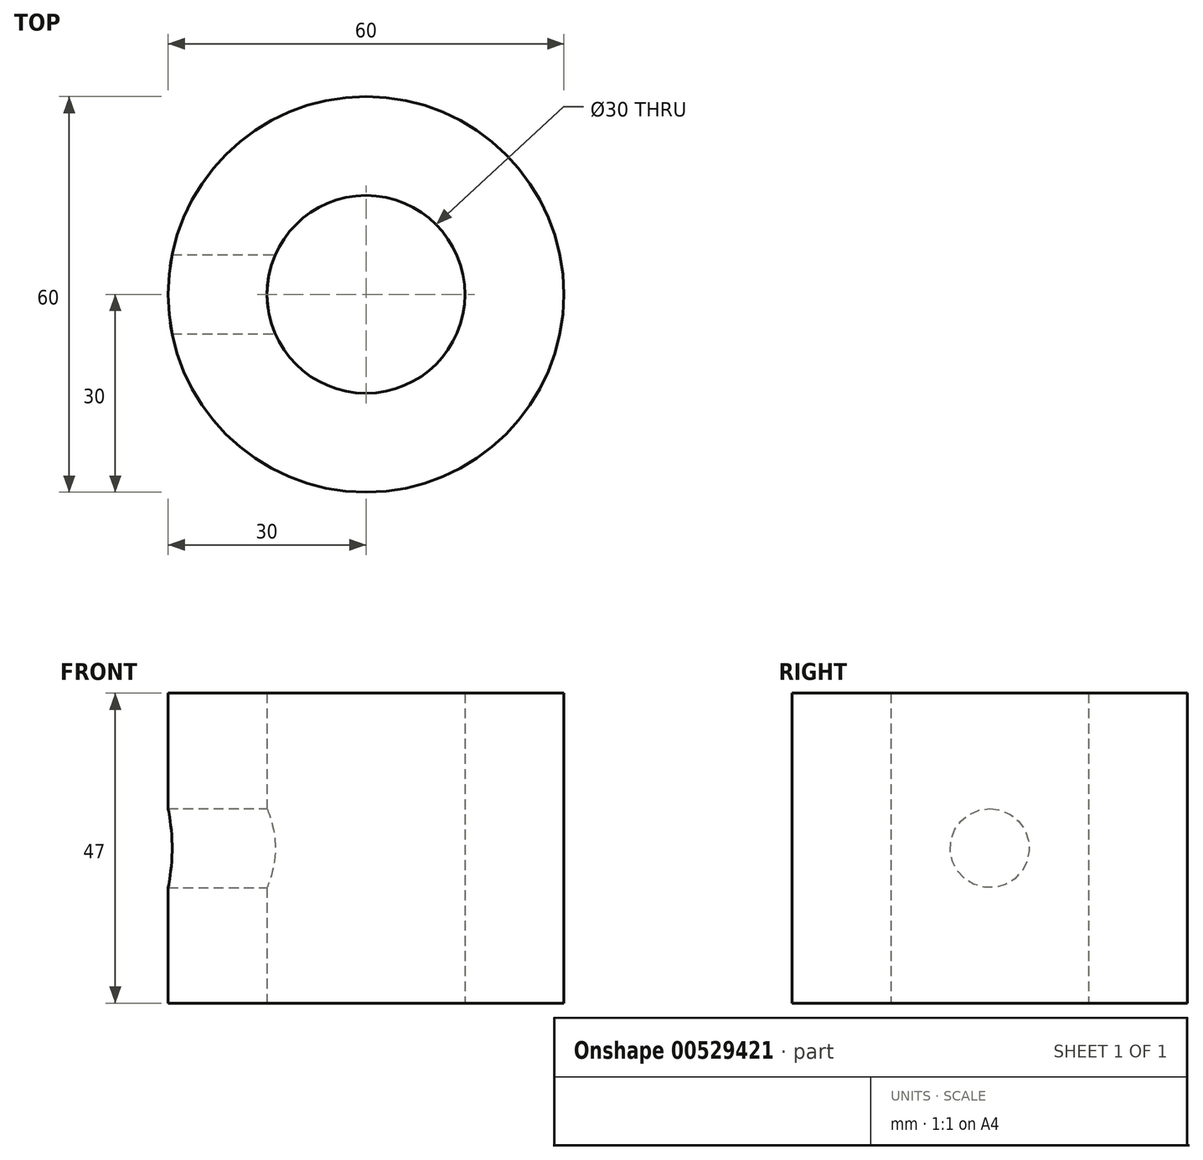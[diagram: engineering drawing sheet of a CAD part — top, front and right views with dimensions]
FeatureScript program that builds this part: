
annotation { "Feature Type Name" : "Feature", "Feature Type Description" : "" }
export const myFeature = defineFeature(function(context is Context, id is Id, definition is map)
    precondition{}
    {
        {
            var Q0;
            Q0=qCreatedBy(makeId("Top.planeOp"),FACE);
            var sketch = newSketch(context, id + "F0", { "sketchPlane" : qUnion([Q0])});
            skCircle(sketch, "E0", {"center": v(0, 0) * mm, "radius": 15 * mm});
            skCircle(sketch, "E1", {"center": v(0, 0) * mm, "radius": 30 * mm});
            skSolve(sketch);
        }
        {
            var Q0;
            Q0=makeQuery(id+"F0.imprint","IMPRINT",FACE,{"disambiguationData":[TD([[makeQuery(id+"F0.imprint","IMPRINT",EDGE,{"derivedFrom":sQuery(id+"F0.wireOp",EDGE,"E0")}),-1.0]])]});
            extrude(context, id + "F1", {"entities" : qUnion([Q0]), "depth" : 47 * mm, "offsetDistance" : 25 * mm});
        }
        {
            var Q0;
            Q0=qCreatedBy(makeId("Right.planeOp"),FACE);
            var sketch = newSketch(context, id + "F2", { "sketchPlane" : qUnion([Q0])});
            skLineSegment(sketch, "E2.0", {"start": v(-30, 47) * mm, "end": v(30, 47) * mm});
            skLineSegment(sketch, "E3", {"start": v(0, 0) * mm, "end": v(0, 23.5) * mm, "construction": true});
            skPoint(sketch, "E4", {"position": v(0, 23.5) * mm});
            skLineSegment(sketch, "E5", {"start": v(0, 23.5) * mm, "end": v(0, 47) * mm, "construction": true});
            skSolve(sketch);
        }
        {
            var Q0;
            Q0=sQuery(id+"F2.wireOp",VERTEX,"E4");
            var Q1;
            Q1=makeQuery(id+"F1.opExtrude","SWEPT_BODY",BODY,{"disambiguationData":[OSD([sQuery(id+"F0.wireOp",EDGE,"E0"),sQuery(id+"F0.wireOp",EDGE,"E1")])]});
            hole(context, id + "F3", {"style" : HoleStyle.SIMPLE, "endStyle" : HoleEndStyle.BLIND, "holeDiameter" : 12 * mm, "holeDepth" : 30 * mm, "isTappedThrough" : true, "tappedDepth" : 12 * mm, "tapClearance" : 3, "locations" : qUnion([Q0]), "scope" : qUnion([Q1])});
        }
    });
